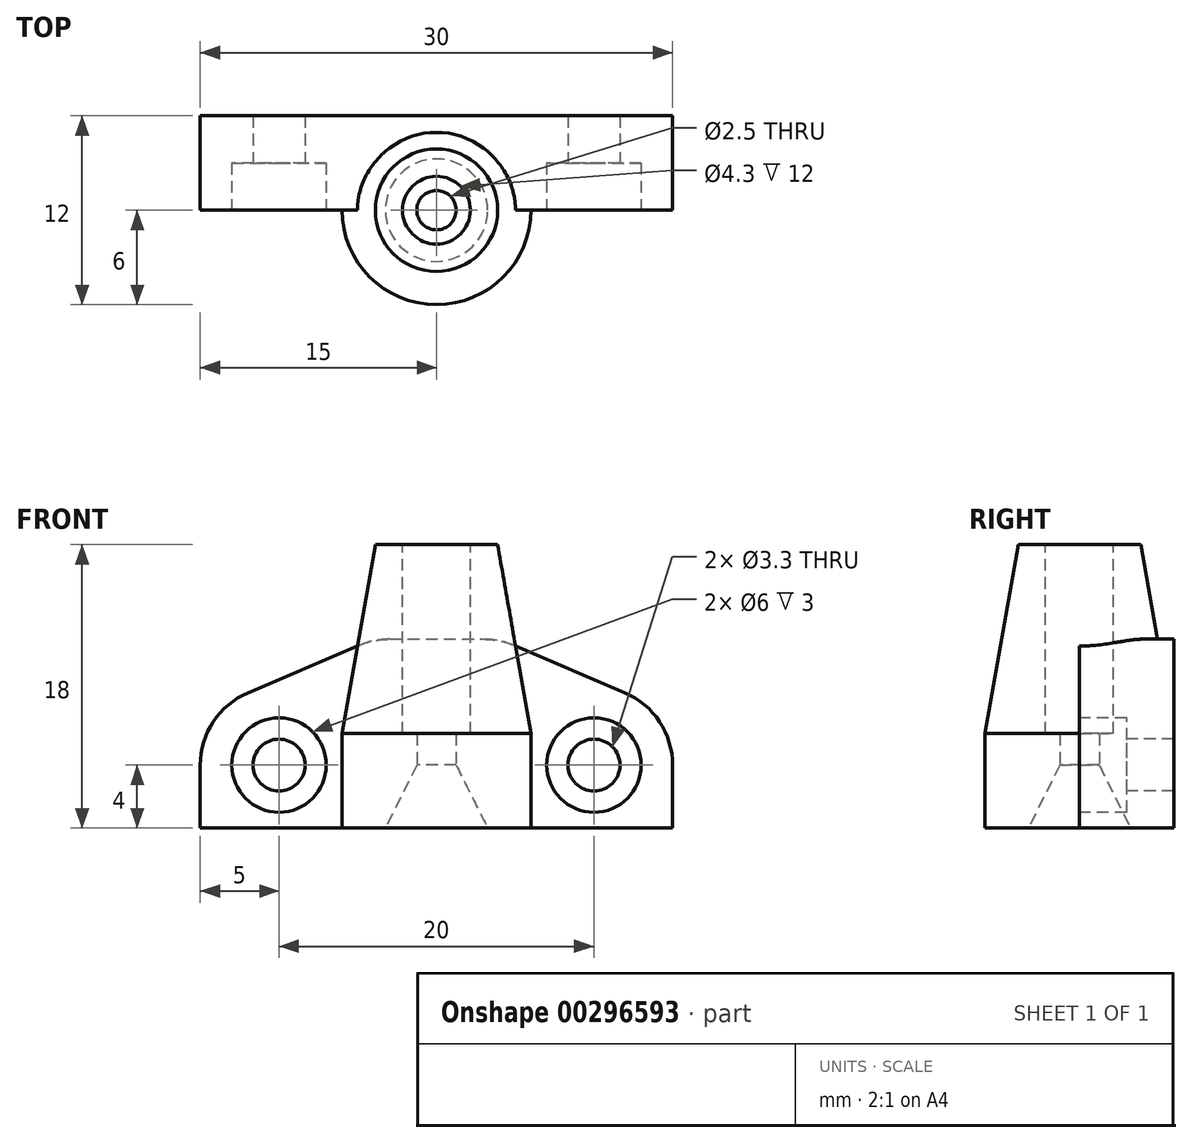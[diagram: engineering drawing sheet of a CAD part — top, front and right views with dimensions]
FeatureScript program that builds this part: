
annotation { "Feature Type Name" : "Feature", "Feature Type Description" : "" }
export const myFeature = defineFeature(function(context is Context, id is Id, definition is map)
    precondition{}
    {
        {
            var Q0;
            Q0=qCreatedBy(makeId("Front.planeOp"),FACE);
            var sketch = newSketch(context, id + "F0", { "sketchPlane" : qUnion([Q0])});
            skLineSegment(sketch, "E0", {"start": v(0, 0) * mm, "end": v(0, 20) * mm, "construction": true});
            skLineSegment(sketch, "E1.0", {"start": v(22, 0) * mm, "end": v(22, 20) * mm});
            skLineSegment(sketch, "E2.0", {"start": v(-22, 0) * mm, "end": v(-22, 20) * mm});
            skSolve(sketch);
        }
        {
            var Q0;
            Q0=qCreatedBy(makeId("Front.planeOp"),FACE);
            var sketch = newSketch(context, id + "F1", { "sketchPlane" : qUnion([Q0])});
            skLineSegment(sketch, "E3", {"start": v(0, 4) * mm, "end": v(10, 4) * mm, "construction": true});
            skLineSegment(sketch, "E4", {"start": v(0, 4) * mm, "end": v(-10, 4) * mm, "construction": true});
            skCircle(sketch, "E5", {"center": v(-10, 4) * mm, "radius": 1.65 * mm});
            skCircle(sketch, "E6", {"center": v(10, 4) * mm, "radius": 1.65 * mm});
            skArc(sketch, "E7", {"start": v(15, 4) * mm, "mid": v(14.17, 6.75) * mm, "end": v(11.96, 8.6) * mm});
            skArc(sketch, "E8", {"start": v(-11.96, 8.6) * mm, "mid": v(-14.17, 6.75) * mm, "end": v(-15, 4) * mm});
            skLineSegment(sketch, "E9", {"start": v(0, 0) * mm, "end": v(0, 12) * mm, "construction": true});
            skLineSegment(sketch, "E10", {"start": v(-4.94, 11.6) * mm, "end": v(-11.96, 8.6) * mm});
            skLineSegment(sketch, "E11", {"start": v(4.94, 11.6) * mm, "end": v(11.96, 8.6) * mm});
            skLineSegment(sketch, "E12", {"start": v(-15, 4) * mm, "end": v(-15, 0) * mm});
            skLineSegment(sketch, "E13", {"start": v(15, 4) * mm, "end": v(15, 0) * mm});
            skPoint(sketch, "E14.orphan", {"position": v(10, -1) * mm});
            skPoint(sketch, "E15.orphan", {"position": v(-10, -1) * mm});
            skLineSegment(sketch, "E16", {"start": v(0, 0) * mm, "end": v(-15, 0) * mm});
            skLineSegment(sketch, "E17", {"start": v(0, 0) * mm, "end": v(15, 0) * mm});
            skLineSegment(sketch, "E18", {"start": v(0, 12) * mm, "end": v(-2.98, 12) * mm});
            skLineSegment(sketch, "E19", {"start": v(0, 12) * mm, "end": v(2.98, 12) * mm});
            skPoint(sketch, "E20.visualSharp", {"position": v(-4, 12) * mm});
            skArc(sketch, "E20.filletArc", {"start": v(-2.98, 12) * mm, "mid": v(-3.98, 11.9) * mm, "end": v(-4.94, 11.6) * mm});
            skPoint(sketch, "E21.visualSharp", {"position": v(4, 12) * mm});
            skArc(sketch, "E21.filletArc", {"start": v(4.94, 11.6) * mm, "mid": v(3.98, 11.9) * mm, "end": v(2.98, 12) * mm});
            skSolve(sketch);
        }
        {
            var Q0;
            Q0 = qSketchRegion(id + "F1", true);
            extrude(context, id + "F2", {"entities" : qUnion([Q0]), "oppositeDirection" : true, "depth" : 6 * mm});
        }
        {
            var Q0;
            Q0=makeQuery(id+"F2.opExtrude","SWEPT_FACE",FACE,{"disambiguationData":[OSD([sQuery(id+"F1.wireOp",EDGE,"E18"),sQuery(id+"F1.wireOp",EDGE,"E19")])]});
            var sketch = newSketch(context, id + "F3", { "sketchPlane" : qUnion([Q0])});
            skCircle(sketch, "E22", {"center": v(0, 0) * mm, "radius": 3.75 * mm});
            skSolve(sketch);
        }
        {
            var Q0;
            Q0 = qSketchRegion(id + "F3", true);
            extrude(context, id + "F4", {"entities" : qUnion([Q0]), "operationType" : NewBodyOperationType.REMOVE, "endBound" : BoundingType.THROUGH_ALL, "oppositeDirection" : true, "depth" : 25 * mm});
        }
        {
            var Q0;
            Q0=qCreatedBy(makeId("Top.planeOp"),FACE);
            var sketch = newSketch(context, id + "F5", { "sketchPlane" : qUnion([Q0])});
            skCircle(sketch, "E23", {"center": v(0, 0) * mm, "radius": 1.25 * mm});
            skCircle(sketch, "E24", {"center": v(0, 0) * mm, "radius": 6 * mm});
            skSolve(sketch);
        }
        {
            var Q0;
            Q0 = qSketchRegion(id + "F5", true);
            extrude(context, id + "F6", {"entities" : qUnion([Q0]), "depth" : 6 * mm});
        }
        {
            var Q0;
            Q0=makeQuery(id+"F6.opExtrude","CAP_EDGE",EDGE,{"disambiguationData":[OSD([sQuery(id+"F5.wireOp",EDGE,"E23")])],"isStart":true});
            chamfer(context, id + "F7", {"entities" : qUnion([Q0]), "chamferType" : ChamferType.TWO_OFFSETS, "width1" : 2 * mm, "oppositeDirection" : false, "width2" : 4 * mm, "tangentPropagation" : true});
        }
        {
            var Q0;
            Q0=makeQuery(id+"F6.opExtrude","CAP_FACE",FACE,{"disambiguationData":[OSD([sQuery(id+"F5.wireOp",EDGE,"E23"),sQuery(id+"F5.wireOp",EDGE,"E24")])],"isStart":false});
            var sketch = newSketch(context, id + "F8", { "sketchPlane" : qUnion([Q0])});
            skCircle(sketch, "E25", {"center": v(0, 0) * mm, "radius": 6 * mm});
            skSolve(sketch);
        }
        {
            var Q0;
            Q0 = qSketchRegion(id + "F8", true);
            extrude(context, id + "F9", {"entities" : qUnion([Q0]), "operationType" : NewBodyOperationType.ADD, "depth" : 12 * mm, "hasDraft" : true, "draftAngle" : 10 * degree, "draftPullDirection" : true});
        }
        {
            var Q0;
            Q0=makeQuery(id+"F9.opExtrude","CAP_FACE",FACE,{"disambiguationData":[OSD([sQuery(id+"F8.wireOp",EDGE,"E25")])],"isStart":false});
            var sketch = newSketch(context, id + "F10", { "sketchPlane" : qUnion([Q0])});
            skCircle(sketch, "E26", {"center": v(0, 0) * mm, "radius": 2.15 * mm});
            skSolve(sketch);
        }
        {
            var Q0;
            Q0 = qSketchRegion(id + "F10", true);
            extrude(context, id + "F11", {"entities" : qUnion([Q0]), "operationType" : NewBodyOperationType.REMOVE, "oppositeDirection" : true, "depth" : 12 * mm});
        }
        {
            var Q0;
            {var subQ0=sQuery(id+"F1.wireOp",EDGE,"E12");var subQ1=sQuery(id+"F1.wireOp",EDGE,"E10");var subQ2=sQuery(id+"F1.wireOp",EDGE,"E8");var subQ3=sQuery(id+"F1.wireOp",EDGE,"E5");var subQ4=sQuery(id+"F1.wireOp",EDGE,"E17");var subQ5=sQuery(id+"F1.wireOp",EDGE,"E16");var subQ6=sQuery(id+"F1.wireOp",EDGE,"E20.filletArc");Q0=makeQuery(id+"F4.boolean.opBoolean","SPLIT",FACE,{"disambiguationData":[TD([makeQuery(id+"F2.opExtrude","SWEPT_FACE",FACE,{"disambiguationData":[OSD([subQ3])]})])],"derivedFrom":makeQuery(id+"F2.opExtrude","CAP_FACE",FACE,{"disambiguationData":[OSD([subQ3,sQuery(id+"F1.wireOp",EDGE,"E6"),sQuery(id+"F1.wireOp",EDGE,"E7"),subQ2,subQ1,sQuery(id+"F1.wireOp",EDGE,"E11"),subQ0,sQuery(id+"F1.wireOp",EDGE,"E13"),subQ5,subQ4,sQuery(id+"F1.wireOp",EDGE,"E18"),sQuery(id+"F1.wireOp",EDGE,"E19"),subQ6,sQuery(id+"F1.wireOp",EDGE,"E21.filletArc")])],"isStart":true})});}
            var sketch = newSketch(context, id + "F12", { "sketchPlane" : qUnion([Q0])});
            skCircle(sketch, "E27", {"center": v(-10, 4) * mm, "radius": 3 * mm});
            skSolve(sketch);
        }
        {
            var Q0;
            Q0 = qSketchRegion(id + "F12", true);
            extrude(context, id + "F13", {"entities" : qUnion([Q0]), "operationType" : NewBodyOperationType.REMOVE, "oppositeDirection" : true, "depth" : 3 * mm});
        }
        {
            var Q0;
            {var subQ0=sQuery(id+"F1.wireOp",EDGE,"E11");var subQ1=sQuery(id+"F1.wireOp",EDGE,"E13");var subQ2=sQuery(id+"F1.wireOp",EDGE,"E7");var subQ3=sQuery(id+"F1.wireOp",EDGE,"E6");var subQ4=sQuery(id+"F1.wireOp",EDGE,"E17");var subQ5=sQuery(id+"F1.wireOp",EDGE,"E16");var subQ6=sQuery(id+"F1.wireOp",EDGE,"E21.filletArc");Q0=makeQuery(id+"F4.boolean.opBoolean","SPLIT",FACE,{"disambiguationData":[TD([makeQuery(id+"F2.opExtrude","SWEPT_FACE",FACE,{"disambiguationData":[OSD([subQ3])]})])],"derivedFrom":makeQuery(id+"F2.opExtrude","CAP_FACE",FACE,{"disambiguationData":[OSD([sQuery(id+"F1.wireOp",EDGE,"E5"),subQ3,subQ2,sQuery(id+"F1.wireOp",EDGE,"E8"),sQuery(id+"F1.wireOp",EDGE,"E10"),subQ0,sQuery(id+"F1.wireOp",EDGE,"E12"),subQ1,subQ5,subQ4,sQuery(id+"F1.wireOp",EDGE,"E18"),sQuery(id+"F1.wireOp",EDGE,"E19"),sQuery(id+"F1.wireOp",EDGE,"E20.filletArc"),subQ6])],"isStart":true})});}
            var sketch = newSketch(context, id + "F14", { "sketchPlane" : qUnion([Q0])});
            skCircle(sketch, "E28", {"center": v(10, 4) * mm, "radius": 3 * mm});
            skSolve(sketch);
        }
        {
            var Q0;
            Q0 = qSketchRegion(id + "F14", true);
            extrude(context, id + "F15", {"entities" : qUnion([Q0]), "operationType" : NewBodyOperationType.REMOVE, "oppositeDirection" : true, "depth" : 3 * mm});
        }
    });
